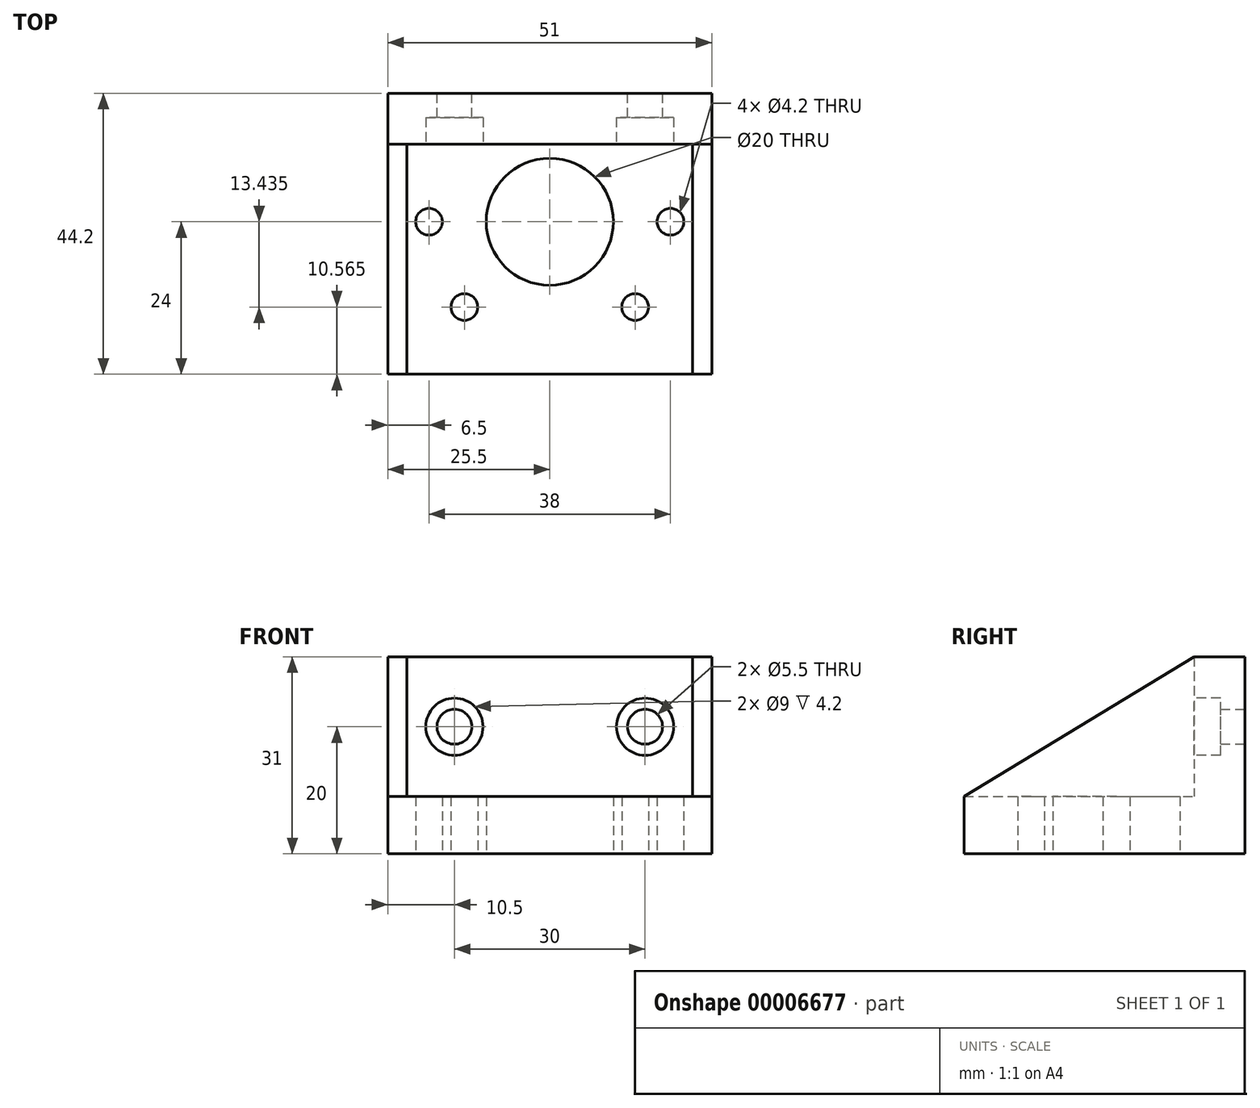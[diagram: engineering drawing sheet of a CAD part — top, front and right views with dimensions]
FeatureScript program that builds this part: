
annotation { "Feature Type Name" : "Feature", "Feature Type Description" : "" }
export const myFeature = defineFeature(function(context is Context, id is Id, definition is map)
    precondition{}
    {
        {
            var Q0;
            Q0=qCreatedBy(makeId("Top.planeOp"),FACE);
            var sketch = newSketch(context, id + "F0", { "sketchPlane" : qUnion([Q0])});
            skLineSegment(sketch, "E0.bottom", {"start": v(0, 0) * mm, "end": v(51, 0) * mm});
            skLineSegment(sketch, "E0.top", {"start": v(0, 44.2) * mm, "end": v(51, 44.2) * mm});
            skLineSegment(sketch, "E0.left", {"start": v(0, 0) * mm, "end": v(0, 44.2) * mm});
            skLineSegment(sketch, "E0.right", {"start": v(51, 0) * mm, "end": v(51, 44.2) * mm});
            skSolve(sketch);
        }
        {
            var Q0;
            Q0=qSketchRegion(id+"F0",true);
            extrude(context, id + "F1", {"entities" : qUnion([Q0]), "depth" : 9 * mm});
        }
        {
            var Q0;
            Q0=makeQuery(id+"F1.opExtrude","CAP_FACE",FACE,{"disambiguationData":[OSD([sQuery(id+"F0.wireOp",EDGE,"E0.bottom"),sQuery(id+"F0.wireOp",EDGE,"E0.top"),sQuery(id+"F0.wireOp",EDGE,"E0.left"),sQuery(id+"F0.wireOp",EDGE,"E0.right")])],"isStart":false});
            var sketch = newSketch(context, id + "F2", { "sketchPlane" : qUnion([Q0])});
            skLineSegment(sketch, "E1.bottom", {"start": v(0, 44.2) * mm, "end": v(51, 44.2) * mm});
            skLineSegment(sketch, "E1.top", {"start": v(0, 36.2) * mm, "end": v(51, 36.2) * mm});
            skLineSegment(sketch, "E1.left", {"start": v(0, 44.2) * mm, "end": v(0, 36.2) * mm});
            skLineSegment(sketch, "E1.right", {"start": v(51, 44.2) * mm, "end": v(51, 36.2) * mm});
            skSolve(sketch);
        }
        {
            var Q0;
            Q0=qSketchRegion(id+"F2",true);
            extrude(context, id + "F3", {"entities" : qUnion([Q0]), "operationType" : NewBodyOperationType.ADD, "depth" : 22 * mm});
        }
        {
            var Q0;
            Q0=makeQuery(id+"F3.boolean.opBoolean","MERGE",FACE,{"derivedFrom":[makeQuery(id+"F1.opExtrude","SWEPT_FACE",FACE,{"disambiguationData":[OSD([sQuery(id+"F0.wireOp",EDGE,"E0.right")])]}),makeQuery(id+"F3.opExtrude","SWEPT_FACE",FACE,{"disambiguationData":[OSD([sQuery(id+"F2.wireOp",EDGE,"E1.right")])]})]});
            var sketch = newSketch(context, id + "F4", { "sketchPlane" : qUnion([Q0])});
            skLineSegment(sketch, "E2", {"start": v(36.2, 31) * mm, "end": v(0, 9) * mm});
            skLineSegment(sketch, "E3", {"start": v(0, 9) * mm, "end": v(36.2, 9) * mm});
            skLineSegment(sketch, "E4", {"start": v(36.2, 9) * mm, "end": v(36.2, 31) * mm});
            skSolve(sketch);
        }
        {
            var Q0;
            Q0=qSketchRegion(id+"F4",true);
            extrude(context, id + "F5", {"entities" : qUnion([Q0]), "operationType" : NewBodyOperationType.ADD, "oppositeDirection" : true, "depth" : 3 * mm});
        }
        {
            var Q0;
            Q0=makeQuery(id+"F3.boolean.opBoolean","MERGE",FACE,{"derivedFrom":[makeQuery(id+"F1.opExtrude","SWEPT_FACE",FACE,{"disambiguationData":[OSD([sQuery(id+"F0.wireOp",EDGE,"E0.left")])]}),makeQuery(id+"F3.opExtrude","SWEPT_FACE",FACE,{"disambiguationData":[OSD([sQuery(id+"F2.wireOp",EDGE,"E1.left")])]})]});
            var sketch = newSketch(context, id + "F6", { "sketchPlane" : qUnion([Q0])});
            skLineSegment(sketch, "E5", {"start": v(0, 9) * mm, "end": v(-36.2, 9) * mm});
            skLineSegment(sketch, "E6", {"start": v(-36.2, 9) * mm, "end": v(-36.2, 31) * mm});
            skLineSegment(sketch, "E7", {"start": v(-36.2, 31) * mm, "end": v(0, 9) * mm});
            skSolve(sketch);
        }
        {
            var Q0;
            Q0=qSketchRegion(id+"F6",true);
            extrude(context, id + "F7", {"entities" : qUnion([Q0]), "operationType" : NewBodyOperationType.ADD, "oppositeDirection" : true, "depth" : 3 * mm});
        }
        {
            var Q0;
            Q0=makeQuery(id+"F3.boolean.opBoolean","MERGE",FACE,{"derivedFrom":[makeQuery(id+"F1.opExtrude","SWEPT_FACE",FACE,{"disambiguationData":[OSD([sQuery(id+"F0.wireOp",EDGE,"E0.top")])]}),makeQuery(id+"F3.opExtrude","SWEPT_FACE",FACE,{"disambiguationData":[OSD([sQuery(id+"F2.wireOp",EDGE,"E1.bottom")])]})]});
            var sketch = newSketch(context, id + "F8", { "sketchPlane" : qUnion([Q0])});
            skCircle(sketch, "E8", {"center": v(-40.5, 20) * mm, "radius": 2.75 * mm});
            skCircle(sketch, "E9", {"center": v(-10.5, 20) * mm, "radius": 2.75 * mm});
            skSolve(sketch);
        }
        {
            var Q0;
            Q0=qSketchRegion(id+"F8",true);
            extrude(context, id + "F9", {"entities" : qUnion([Q0]), "operationType" : NewBodyOperationType.REMOVE, "endBound" : BoundingType.THROUGH_ALL, "oppositeDirection" : true, "depth" : 25 * mm});
        }
        {
            var Q0;
            Q0=makeQuery(id+"F1.opExtrude","CAP_FACE",FACE,{"disambiguationData":[OSD([sQuery(id+"F0.wireOp",EDGE,"E0.bottom"),sQuery(id+"F0.wireOp",EDGE,"E0.top"),sQuery(id+"F0.wireOp",EDGE,"E0.left"),sQuery(id+"F0.wireOp",EDGE,"E0.right")])],"isStart":true});
            var sketch = newSketch(context, id + "F10", { "sketchPlane" : qUnion([Q0])});
            skCircle(sketch, "E10", {"center": v(25.5, -24) * mm, "radius": 10 * mm});
            skCircle(sketch, "E11", {"center": v(25.5, -24) * mm, "radius": 19 * mm, "construction": true});
            skLineSegment(sketch, "E12", {"start": v(25.5, -24) * mm, "end": v(44.5, -24) * mm, "construction": true});
            skLineSegment(sketch, "E13", {"start": v(25.5, -24) * mm, "end": v(6.5, -24) * mm, "construction": true});
            skLineSegment(sketch, "E14", {"start": v(25.5, -24) * mm, "end": v(44.32, -5.18) * mm, "construction": true});
            skLineSegment(sketch, "E15", {"start": v(4.5, -3) * mm, "end": v(25.5, -24) * mm, "construction": true});
            skCircle(sketch, "E16", {"center": v(38.94, -10.56) * mm, "radius": 2.1 * mm});
            skCircle(sketch, "E17", {"center": v(44.5, -24) * mm, "radius": 2.1 * mm});
            skCircle(sketch, "E18", {"center": v(6.5, -24) * mm, "radius": 2.1 * mm});
            skCircle(sketch, "E19", {"center": v(12.06, -10.56) * mm, "radius": 2.1 * mm});
            skSolve(sketch);
        }
        {
            var Q0;
            Q0=qSketchRegion(id+"F10",true);
            extrude(context, id + "F11", {"entities" : qUnion([Q0]), "operationType" : NewBodyOperationType.REMOVE, "endBound" : BoundingType.THROUGH_ALL, "oppositeDirection" : true, "depth" : 25 * mm});
        }
        {
            var Q0;
            {var subQ0=sQuery(id+"F2.wireOp",EDGE,"E1.top");var subQ1=sQuery(id+"F6.wireOp",EDGE,"E7");Q0=makeQuery(id+"F11.boolean.opBoolean","SPLIT",FACE,{"disambiguationData":[TD([makeQuery(id+"F7.opExtrude","SWEPT_FACE",FACE,{"disambiguationData":[OSD([subQ1])]})])],"derivedFrom":makeQuery(id+"F3.opExtrude","SWEPT_FACE",FACE,{"disambiguationData":[OSD([subQ0])]})});}
            var sketch = newSketch(context, id + "F12", { "sketchPlane" : qUnion([Q0])});
            skCircle(sketch, "E20", {"center": v(10.5, 20) * mm, "radius": 4.5 * mm});
            skSolve(sketch);
        }
        {
            var Q0;
            Q0=qSketchRegion(id+"F12",true);
            extrude(context, id + "F13", {"entities" : qUnion([Q0]), "operationType" : NewBodyOperationType.REMOVE, "oppositeDirection" : true, "depth" : 4.2 * mm});
        }
        {
            var Q0;
            {var subQ0=sQuery(id+"F2.wireOp",EDGE,"E1.top");var subQ1=sQuery(id+"F4.wireOp",EDGE,"E2");Q0=makeQuery(id+"F11.boolean.opBoolean","SPLIT",FACE,{"disambiguationData":[TD([makeQuery(id+"F5.opExtrude","SWEPT_FACE",FACE,{"disambiguationData":[OSD([subQ1])]})])],"derivedFrom":makeQuery(id+"F3.opExtrude","SWEPT_FACE",FACE,{"disambiguationData":[OSD([subQ0])]})});}
            var sketch = newSketch(context, id + "F14", { "sketchPlane" : qUnion([Q0])});
            skCircle(sketch, "E21", {"center": v(40.5, 20) * mm, "radius": 4.5 * mm});
            skSolve(sketch);
        }
        {
            var Q0;
            Q0=qSketchRegion(id+"F14",true);
            extrude(context, id + "F15", {"entities" : qUnion([Q0]), "operationType" : NewBodyOperationType.REMOVE, "oppositeDirection" : true, "depth" : 4.2 * mm});
        }
    });
